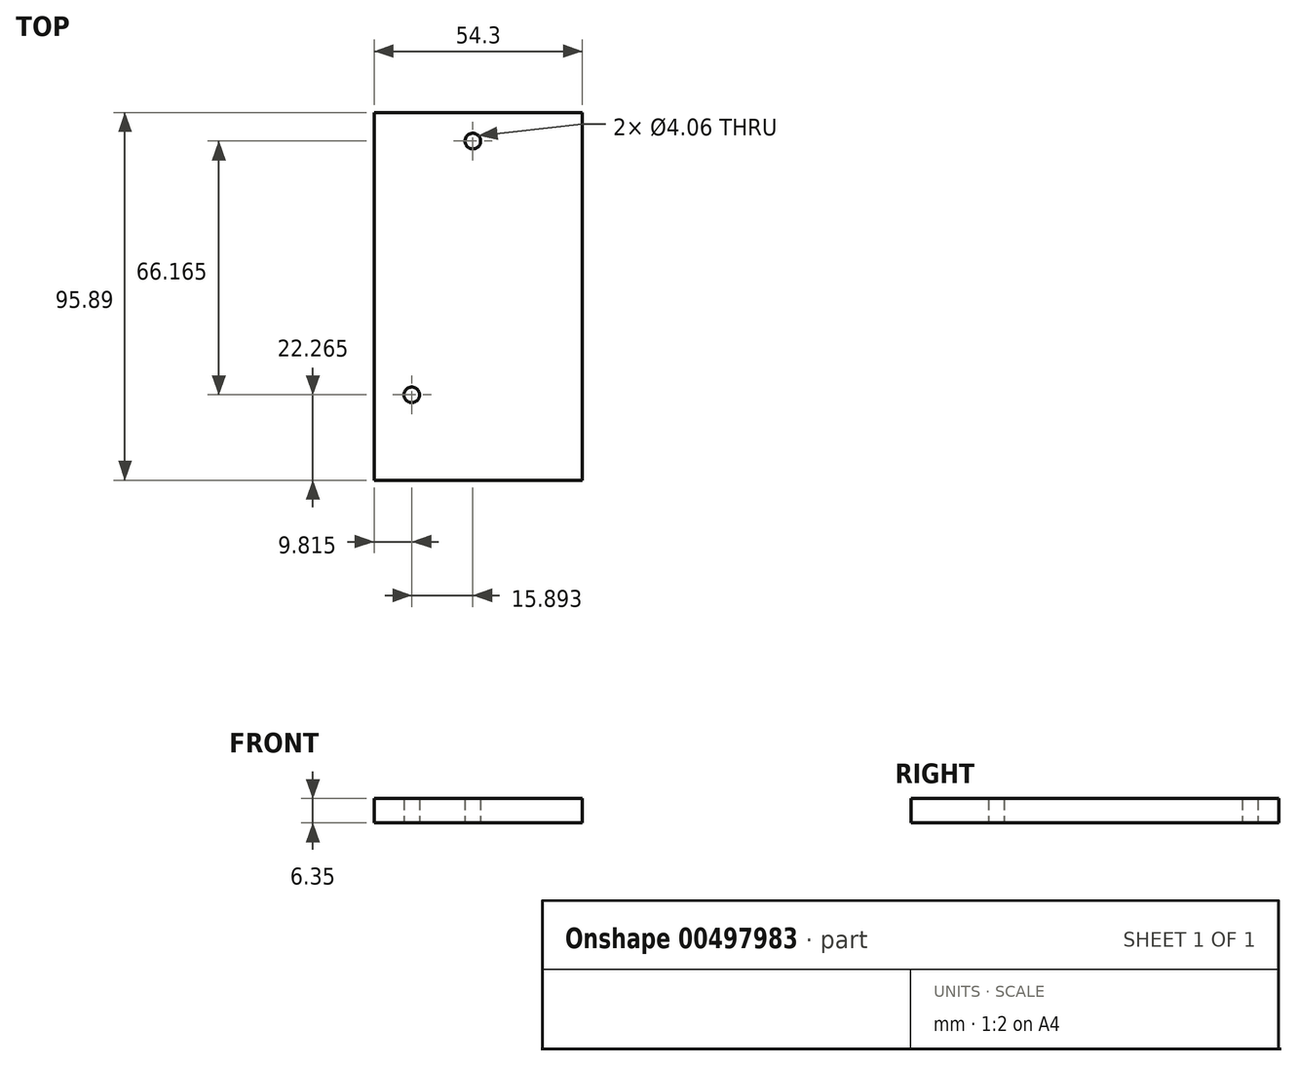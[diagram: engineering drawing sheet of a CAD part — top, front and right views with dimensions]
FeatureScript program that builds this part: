
annotation { "Feature Type Name" : "Feature", "Feature Type Description" : "" }
export const myFeature = defineFeature(function(context is Context, id is Id, definition is map)
    precondition{}
    {
        {
            var Q0;
            Q0=qCreatedBy(makeId("Top.planeOp"),FACE);
            var sketch = newSketch(context, id + "F0", { "sketchPlane" : qUnion([Q0])});
            skPoint(sketch, "E0.middle", {"position": v(0, -2.57) * mm});
            skLineSegment(sketch, "E1.bottom", {"start": v(36.69, 25.35) * mm, "end": v(57.65, 25.35) * mm});
            skLineSegment(sketch, "E1.top", {"start": v(36.69, -16.91) * mm, "end": v(57.65, -16.91) * mm});
            skLineSegment(sketch, "E1.left", {"start": v(36.69, 25.35) * mm, "end": v(36.69, -16.91) * mm});
            skLineSegment(sketch, "E1.right", {"start": v(57.65, 25.35) * mm, "end": v(57.65, -16.91) * mm});
            skCircle(sketch, "E2", {"center": v(-34.61, -4.52) * mm, "radius": 2.03 * mm});
            skCircle(sketch, "E3", {"center": v(-18.72, 61.64) * mm, "radius": 2.03 * mm});
            skCircle(sketch, "E4", {"center": v(32.2, 61.64) * mm, "radius": 2.03 * mm});
            skLineSegment(sketch, "E5", {"start": v(-18.72, 61.64) * mm, "end": v(32.2, 61.64) * mm});
            skLineSegment(sketch, "E6", {"start": v(36.69, 25.35) * mm, "end": v(36.69, 85.85) * mm});
            skLineSegment(sketch, "E7", {"start": v(64.16, 69.1) * mm, "end": v(64.16, -26.8) * mm});
            skLineSegment(sketch, "E8", {"start": v(-44.43, 69.1) * mm, "end": v(-44.43, -26.8) * mm});
            skLineSegment(sketch, "E9", {"start": v(-18.72, 59.6) * mm, "end": v(-18.72, -36.83) * mm});
            skLineSegment(sketch, "E10", {"start": v(64.16, 69.1) * mm, "end": v(-44.43, 69.1) * mm});
            skLineSegment(sketch, "E11", {"start": v(64.16, -26.8) * mm, "end": v(-44.43, -26.8) * mm});
            skLineSegment(sketch, "E12", {"start": v(9.87, -26.8) * mm, "end": v(9.87, 69.1) * mm});
            skSolve(sketch);
        }
        {
            var Q0;
            Q0 = qSketchRegion(id + "F0", true);
            extrude(context, id + "F1", {"entities" : qUnion([Q0]), "depth" : 6.35 * mm, "offsetDistance" : 25.4 * mm});
        }
        {
            var Q0;
            Q0=makeQuery(id+"F1.opExtrude","CAP_FACE",FACE,{"disambiguationData":[OSD([sQuery(id+"F0.wireOp",EDGE,"uhHRWf5C-Bq3m-zUtV-Db8C-2xL5GHQPftrJ.right"),sQuery(id+"F0.wireOp",EDGE,"E1.bottom"),sQuery(id+"F0.wireOp",EDGE,"E1.top"),sQuery(id+"F0.wireOp",EDGE,"E1.left"),sQuery(id+"F0.wireOp",EDGE,"E1.right"),sQuery(id+"F0.wireOp",EDGE,"E2"),sQuery(id+"F0.wireOp",EDGE,"DTK58YUI-AREt-yh4n-3qIi-F3qa293CWWba"),sQuery(id+"F0.wireOp",EDGE,"1oRiDtXn-COO8-dTWl-ABqG-dBbXAhKhDW46"),sQuery(id+"F0.wireOp",EDGE,"tDmWFy9g-Lq8L-EyrD-nrdN-q166ebyH1ysv"),sQuery(id+"F0.wireOp",EDGE,"zQIm1GsK-npcG-IpeT-7j6l-7nQY8yfd2Yrh"),sQuery(id+"F0.wireOp",EDGE,"E3"),sQuery(id+"F0.wireOp",EDGE,"E4")])],"isStart":false});
            var sketch = newSketch(context, id + "F2", { "sketchPlane" : qUnion([Q0])});
            skLineSegment(sketch, "E13.bottom", {"start": v(31.1, 32.87) * mm, "end": v(63.1, 32.87) * mm});
            skLineSegment(sketch, "E13.top", {"start": v(31.1, -24.28) * mm, "end": v(63.1, -24.28) * mm});
            skLineSegment(sketch, "E13.left", {"start": v(31.1, 32.87) * mm, "end": v(31.1, -24.28) * mm});
            skLineSegment(sketch, "E13.right", {"start": v(63.1, 32.87) * mm, "end": v(63.1, -24.28) * mm});
            skLineSegment(sketch, "E14", {"start": v(36.69, 25.35) * mm, "end": v(36.69, -16.91) * mm});
            skLineSegment(sketch, "E15", {"start": v(36.69, -16.91) * mm, "end": v(57.65, -16.91) * mm});
            skLineSegment(sketch, "E16", {"start": v(57.65, -16.91) * mm, "end": v(57.65, 25.35) * mm});
            skLineSegment(sketch, "E17", {"start": v(57.65, 25.35) * mm, "end": v(36.69, 25.35) * mm});
            skSolve(sketch);
        }
        {
            var Q0;
            Q0=makeQuery(id+"F2.imprint","IMPRINT",FACE,{"disambiguationData":[TD([[makeQuery(id+"F2.imprint","IMPRINT",EDGE,{"derivedFrom":sQuery(id+"F2.wireOp",EDGE,"E13.bottom")}),-1.0]])]});
            extrude(context, id + "F3", {"entities" : qUnion([Q0]), "operationType" : NewBodyOperationType.ADD, "depth" : 12.7 * mm, "offsetDistance" : 25.4 * mm});
        }
        {
            var Q0;
            Q0=makeQuery(id+"F1.opExtrude","CAP_FACE",FACE,{"disambiguationData":[OSD([sQuery(id+"F0.wireOp",EDGE,"E1.bottom"),sQuery(id+"F0.wireOp",EDGE,"E1.top"),sQuery(id+"F0.wireOp",EDGE,"E1.left"),sQuery(id+"F0.wireOp",EDGE,"E1.right"),sQuery(id+"F0.wireOp",EDGE,"E2"),sQuery(id+"F0.wireOp",EDGE,"E3"),sQuery(id+"F0.wireOp",EDGE,"E4"),sQuery(id+"F0.wireOp",EDGE,"E7"),sQuery(id+"F0.wireOp",EDGE,"E8"),sQuery(id+"F0.wireOp",EDGE,"E10"),sQuery(id+"F0.wireOp",EDGE,"E11")])],"isStart":false});
            var sketch = newSketch(context, id + "F4", { "sketchPlane" : qUnion([Q0])});
            skLineSegment(sketch, "E18", {"start": v(9.87, 69.1) * mm, "end": v(9.87, -26.8) * mm});
            skLineSegment(sketch, "E19", {"start": v(64.16, 69.1) * mm, "end": v(64.16, -26.8) * mm});
            skLineSegment(sketch, "E20", {"start": v(-44.43, 69.1) * mm, "end": v(-44.43, -26.8) * mm});
            skSolve(sketch);
        }
        {
            var Q0;
            {var subQ2=sQuery(id+"F4.wireOp",EDGE,"E18");Q0=makeQuery(id+"F4.imprint","IMPRINT",FACE,{"disambiguationData":[TD([[makeQuery(id+"F4.imprint","IMPRINT",EDGE,{"derivedFrom":subQ2}),1.0]])]});}
            var Q1;
            Q1=makeQuery(id+"F3.opExtrude","CAP_FACE",FACE,{"disambiguationData":[OSD([sQuery(id+"F2.wireOp",EDGE,"E13.bottom"),sQuery(id+"F2.wireOp",EDGE,"E13.top"),sQuery(id+"F2.wireOp",EDGE,"E13.left"),sQuery(id+"F2.wireOp",EDGE,"E13.right"),sQuery(id+"F2.wireOp",EDGE,"E14"),sQuery(id+"F2.wireOp",EDGE,"E15"),sQuery(id+"F2.wireOp",EDGE,"E16"),sQuery(id+"F2.wireOp",EDGE,"E17")])],"isStart":false});
            extrude(context, id + "F5", {"entities" : qUnion([Q0, Q1]), "operationType" : NewBodyOperationType.REMOVE, "oppositeDirection" : true, "depth" : 25.4 * mm, "offsetDistance" : 25.4 * mm});
        }
    });
